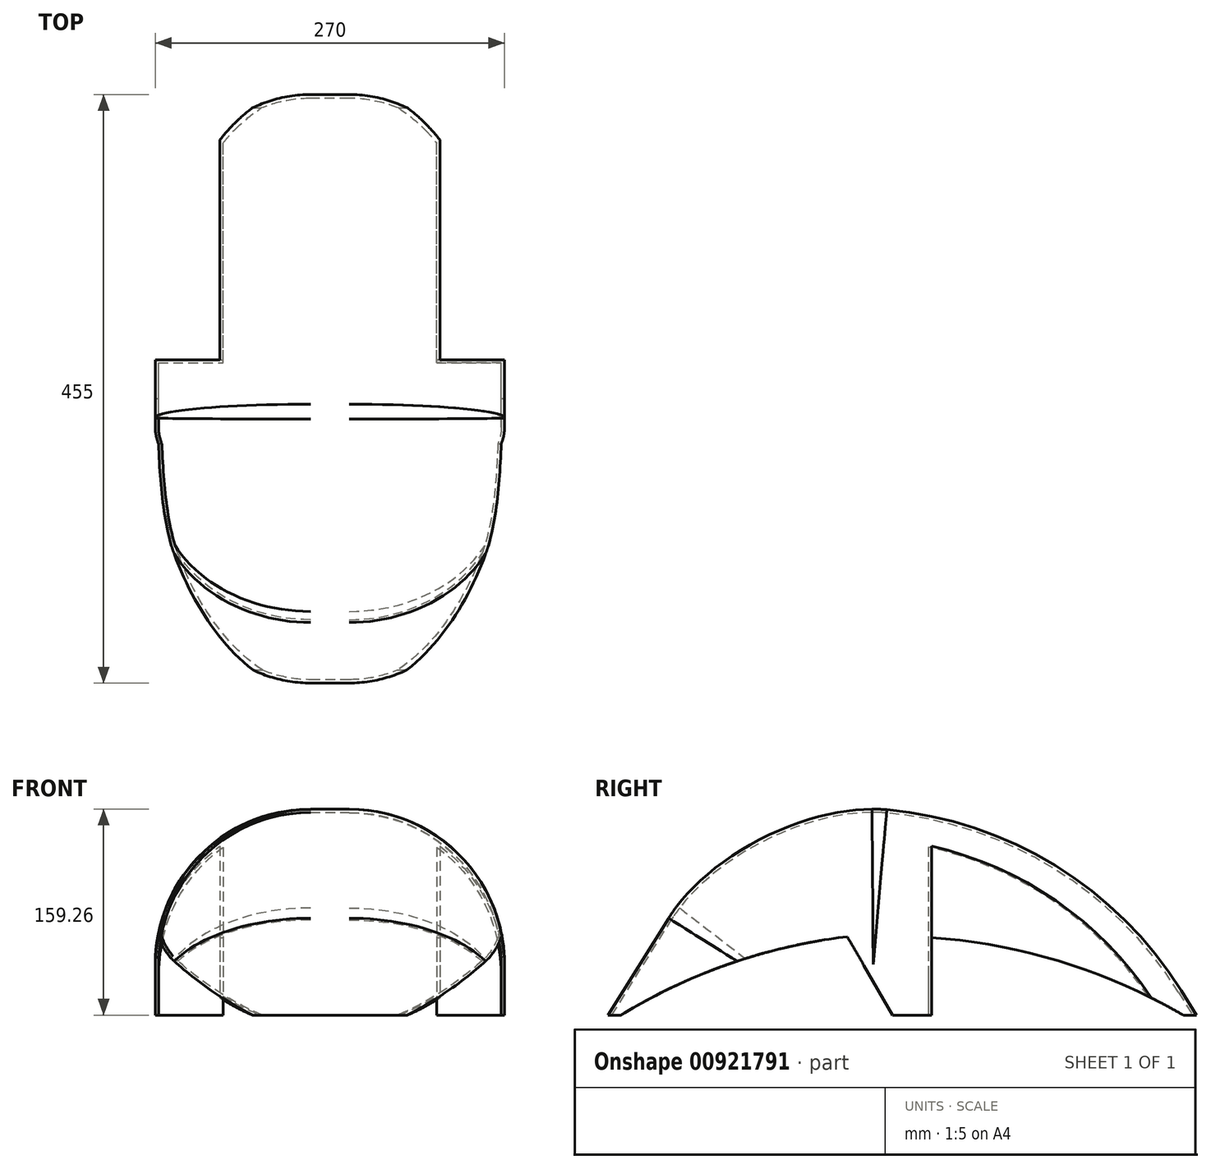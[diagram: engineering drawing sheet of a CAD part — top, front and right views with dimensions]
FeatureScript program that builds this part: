
annotation { "Feature Type Name" : "Feature", "Feature Type Description" : "" }
export const myFeature = defineFeature(function(context is Context, id is Id, definition is map)
    precondition{}
    {
        {
            var Q0;
            Q0=qCreatedBy(makeId("Top.planeOp"),FACE);
            var sketch = newSketch(context, id + "F0", { "sketchPlane" : qUnion([Q0])});
            skLineSegment(sketch, "E0.bottom", {"start": v(135, -227.5) * mm, "end": v(-135, -227.5) * mm});
            skLineSegment(sketch, "E0.top", {"start": v(135, 227.5) * mm, "end": v(-135, 227.5) * mm});
            skLineSegment(sketch, "E0.left", {"start": v(135, -227.5) * mm, "end": v(135, 227.5) * mm});
            skLineSegment(sketch, "E0.right", {"start": v(-135, -227.5) * mm, "end": v(-135, 227.5) * mm});
            skPoint(sketch, "E0.middle", {"position": v(0, 0) * mm});
            skSolve(sketch);
        }
        {
            var Q0;
            Q0 = qSketchRegion(id + "F0", true);
            extrude(context, id + "F1", {"entities" : qUnion([Q0]), "depth" : 160 * mm, "offsetDistance" : 25 * mm});
        }
        {
            var Q0;
            Q0=makeQuery(id+"F1.opExtrude","CAP_EDGE",EDGE,{"disambiguationData":[OSD([sQuery(id+"F0.wireOp",EDGE,"E0.top")])],"isStart":false});
            var Q1;
            Q1=makeQuery(id+"F1.opExtrude","CAP_EDGE",EDGE,{"disambiguationData":[OSD([sQuery(id+"F0.wireOp",EDGE,"E0.bottom")])],"isStart":false});
            chamfer(context, id + "F2", {"entities" : qUnion([Q0, Q1]), "chamferType" : ChamferType.TWO_OFFSETS, "width1" : 100 * mm, "oppositeDirection" : false, "width2" : 160 * mm, "tangentPropagation" : true});
        }
        {
            var Q0;
            {var subQ0=sQuery(id+"F0.wireOp",EDGE,"E0.top");Q0=makeQuery(id+"F2.opChamfer","BLEND_EDGE",EDGE,{"blendedFrom":[makeQuery(id+"F1.opExtrude","CAP_EDGE",EDGE,{"disambiguationData":[OSD([subQ0])],"isStart":false}),makeQuery(id+"F1.opExtrude","CAP_FACE",FACE,{"disambiguationData":[OSD([sQuery(id+"F0.wireOp",EDGE,"E0.bottom"),subQ0,sQuery(id+"F0.wireOp",EDGE,"E0.left"),sQuery(id+"F0.wireOp",EDGE,"E0.right")])],"isStart":false})],"blendedInto":[makeQuery(id+"F1.opExtrude","CAP_FACE",FACE,{"disambiguationData":[OSD([sQuery(id+"F0.wireOp",EDGE,"E0.bottom"),subQ0,sQuery(id+"F0.wireOp",EDGE,"E0.left"),sQuery(id+"F0.wireOp",EDGE,"E0.right")])],"isStart":false})]});}
            fillet(context, id + "F3", {"entities" : qUnion([Q0]), "radius" : 300 * mm, "tangentPropagation" : true, "allowEdgeOverflow" : false});
        }
        {
            var Q0;
            {var subQ0=sQuery(id+"F0.wireOp",EDGE,"E0.bottom");Q0=makeQuery(id+"F2.opChamfer","BLEND_EDGE",EDGE,{"blendedFrom":[makeQuery(id+"F1.opExtrude","CAP_EDGE",EDGE,{"disambiguationData":[OSD([subQ0])],"isStart":false}),makeQuery(id+"F1.opExtrude","CAP_FACE",FACE,{"disambiguationData":[OSD([subQ0,sQuery(id+"F0.wireOp",EDGE,"E0.top"),sQuery(id+"F0.wireOp",EDGE,"E0.left"),sQuery(id+"F0.wireOp",EDGE,"E0.right")])],"isStart":false})],"blendedInto":[makeQuery(id+"F1.opExtrude","CAP_FACE",FACE,{"disambiguationData":[OSD([subQ0,sQuery(id+"F0.wireOp",EDGE,"E0.top"),sQuery(id+"F0.wireOp",EDGE,"E0.left"),sQuery(id+"F0.wireOp",EDGE,"E0.right")])],"isStart":false})]});}
            fillet(context, id + "F4", {"entities" : qUnion([Q0]), "radius" : 180 * mm, "tangentPropagation" : true, "rho" : 0.4, "crossSection" : FilletCrossSection.CONIC, "allowEdgeOverflow" : false});
        }
        {
            var Q0;
            Q0=makeQuery(id+"F1.opExtrude","CAP_FACE",FACE,{"disambiguationData":[OSD([sQuery(id+"F0.wireOp",EDGE,"E0.bottom"),sQuery(id+"F0.wireOp",EDGE,"E0.top"),sQuery(id+"F0.wireOp",EDGE,"E0.left"),sQuery(id+"F0.wireOp",EDGE,"E0.right")])],"isStart":true});
            var sketch = newSketch(context, id + "F5", { "sketchPlane" : qUnion([Q0])});
            skLineSegment(sketch, "E1.bottom", {"start": v(-135, -22.5) * mm, "end": v(-85, -22.5) * mm});
            skLineSegment(sketch, "E1.top", {"start": v(-135, -227.5) * mm, "end": v(-85, -227.5) * mm});
            skLineSegment(sketch, "E1.left", {"start": v(-135, -22.5) * mm, "end": v(-135, -227.5) * mm});
            skLineSegment(sketch, "E1.right", {"start": v(-85, -22.5) * mm, "end": v(-85, -227.5) * mm});
            skLineSegment(sketch, "E2.bottom", {"start": v(135, -22.5) * mm, "end": v(85, -22.5) * mm});
            skLineSegment(sketch, "E2.top", {"start": v(135, -227.5) * mm, "end": v(85, -227.5) * mm});
            skLineSegment(sketch, "E2.left", {"start": v(135, -22.5) * mm, "end": v(135, -227.5) * mm});
            skLineSegment(sketch, "E2.right", {"start": v(85, -22.5) * mm, "end": v(85, -227.5) * mm});
            skSolve(sketch);
        }
        {
            var Q0;
            Q0 = qSketchRegion(id + "F5", true);
            extrude(context, id + "F6", {"entities" : qUnion([Q0]), "operationType" : NewBodyOperationType.REMOVE, "oppositeDirection" : true, "depth" : 500 * mm, "offsetDistance" : 25 * mm});
        }
        {
            var Q0;
            {var subQ0=sQuery(id+"F0.wireOp",EDGE,"E0.left");var subQ1=sQuery(id+"F0.wireOp",EDGE,"E0.bottom");Q0=makeQuery(id+"F4.opFillet","BLEND_EDGE",EDGE,{"blendedFrom":[makeQuery(id+"F2.opChamfer","BLEND_EDGE",EDGE,{"blendedFrom":[makeQuery(id+"F1.opExtrude","CAP_EDGE",EDGE,{"disambiguationData":[OSD([subQ1])],"isStart":false}),makeQuery(id+"F1.opExtrude","CAP_FACE",FACE,{"disambiguationData":[OSD([subQ1,sQuery(id+"F0.wireOp",EDGE,"E0.top"),subQ0,sQuery(id+"F0.wireOp",EDGE,"E0.right")])],"isStart":false})],"blendedInto":[makeQuery(id+"F1.opExtrude","CAP_FACE",FACE,{"disambiguationData":[OSD([subQ1,sQuery(id+"F0.wireOp",EDGE,"E0.top"),subQ0,sQuery(id+"F0.wireOp",EDGE,"E0.right")])],"isStart":false})]}),makeQuery(id+"F1.opExtrude","SWEPT_FACE",FACE,{"disambiguationData":[OSD([subQ0])]})],"blendedInto":[makeQuery(id+"F1.opExtrude","SWEPT_FACE",FACE,{"disambiguationData":[OSD([subQ0])]})]});}
            var Q1;
            {var subQ0=sQuery(id+"F0.wireOp",EDGE,"E0.right");var subQ1=sQuery(id+"F0.wireOp",EDGE,"E0.bottom");Q1=makeQuery(id+"F4.opFillet","BLEND_EDGE",EDGE,{"blendedFrom":[makeQuery(id+"F2.opChamfer","BLEND_EDGE",EDGE,{"blendedFrom":[makeQuery(id+"F1.opExtrude","CAP_EDGE",EDGE,{"disambiguationData":[OSD([subQ1])],"isStart":false}),makeQuery(id+"F1.opExtrude","CAP_FACE",FACE,{"disambiguationData":[OSD([subQ1,sQuery(id+"F0.wireOp",EDGE,"E0.top"),sQuery(id+"F0.wireOp",EDGE,"E0.left"),subQ0])],"isStart":false})],"blendedInto":[makeQuery(id+"F1.opExtrude","CAP_FACE",FACE,{"disambiguationData":[OSD([subQ1,sQuery(id+"F0.wireOp",EDGE,"E0.top"),sQuery(id+"F0.wireOp",EDGE,"E0.left"),subQ0])],"isStart":false})]}),makeQuery(id+"F1.opExtrude","SWEPT_FACE",FACE,{"disambiguationData":[OSD([subQ0])]})],"blendedInto":[makeQuery(id+"F1.opExtrude","SWEPT_FACE",FACE,{"disambiguationData":[OSD([subQ0])]})]});}
            fillet(context, id + "F7", {"entities" : qUnion([Q0, Q1]), "radius" : 120 * mm, "tangentPropagation" : true, "allowEdgeOverflow" : false});
        }
        {
            var Q0;
            Q0=qCreatedBy(makeId("Right.planeOp"),FACE);
            cPlane(context, id + "F8", {"entities" : qUnion([Q0]), "cplaneType" : CPlaneType.OFFSET, "offset" : 150 * mm, "width" : 150 * mm, "height" : 150 * mm});
        }
        {
            var Q0;
            Q0=qCreatedBy(id+"F8.planeOp",FACE);
            var sketch = newSketch(context, id + "F9", { "sketchPlane" : qUnion([Q0])});
            skLineSegment(sketch, "E3", {"start": v(22.5, 0) * mm, "end": v(22.5, 60) * mm});
            skArc(sketch, "E4", {"start": v(217.14, 0) * mm, "mid": v(123.25, 41.13) * mm, "end": v(22.5, 60) * mm});
            skLineSegment(sketch, "E5", {"start": v(22.5, 0) * mm, "end": v(217.14, 0) * mm});
            skLineSegment(sketch, "E6", {"start": v(-217.5, 0) * mm, "end": v(-7.5, 0) * mm});
            skLineSegment(sketch, "E7", {"start": v(-7.5, 0) * mm, "end": v(-42.5, 60.62) * mm});
            skArc(sketch, "E8", {"start": v(-42.5, 60.62) * mm, "mid": v(-133.28, 39.78) * mm, "end": v(-217.5, 0) * mm});
            skSolve(sketch);
        }
        {
            var Q0;
            Q0=makeQuery(id+"F1.opExtrude","CAP_FACE",FACE,{"disambiguationData":[OSD([sQuery(id+"F0.wireOp",EDGE,"E0.bottom"),sQuery(id+"F0.wireOp",EDGE,"E0.top"),sQuery(id+"F0.wireOp",EDGE,"E0.left"),sQuery(id+"F0.wireOp",EDGE,"E0.right")])],"isStart":true});
            shell(context, id + "F10", {"entities" : qUnion([Q0]), "thickness" : 2.5 * mm});
        }
        {
            var Q0;
            Q0=makeQuery(id+"F9.imprint","IMPRINT",FACE,{"disambiguationData":[TD([[makeQuery(id+"F9.imprint","IMPRINT",EDGE,{"derivedFrom":sQuery(id+"F9.wireOp",EDGE,"E3")}),-1.0]])]});
            var Q1;
            Q1=makeQuery(id+"F9.imprint","IMPRINT",FACE,{"disambiguationData":[TD([[makeQuery(id+"F9.imprint","IMPRINT",EDGE,{"derivedFrom":sQuery(id+"F9.wireOp",EDGE,"E6")}),1.0]])]});
            extrude(context, id + "F11", {"entities" : qUnion([Q0, Q1]), "operationType" : NewBodyOperationType.REMOVE, "oppositeDirection" : true, "depth" : 500 * mm, "offsetDistance" : 25 * mm});
        }
    });
